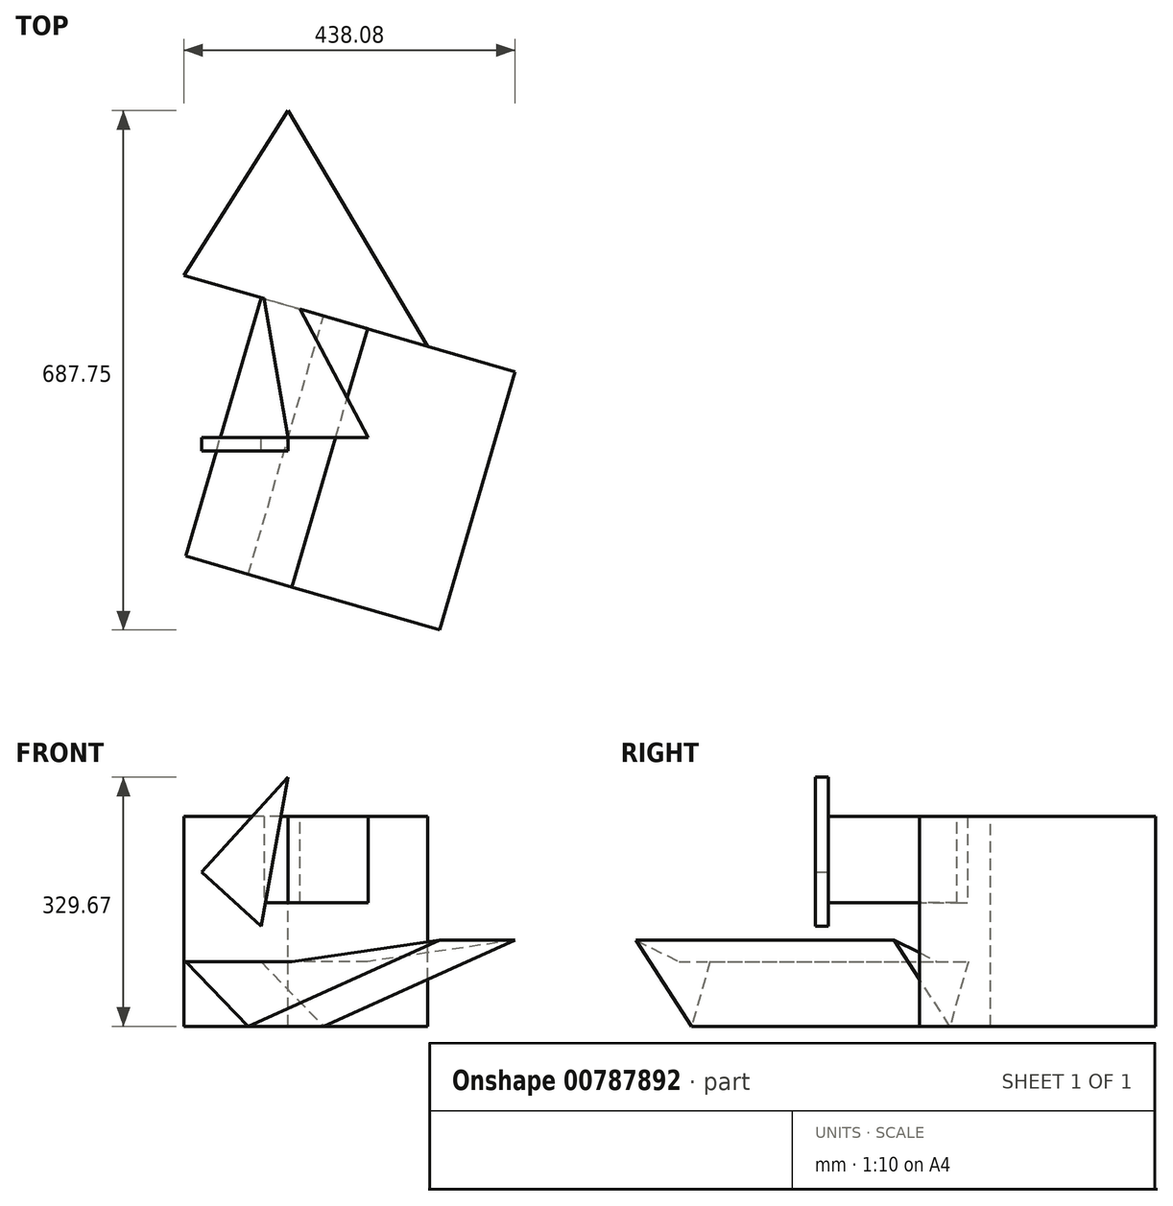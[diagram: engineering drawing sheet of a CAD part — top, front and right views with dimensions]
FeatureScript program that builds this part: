
annotation { "Feature Type Name" : "Feature", "Feature Type Description" : "" }
export const myFeature = defineFeature(function(context is Context, id is Id, definition is map)
    precondition{}
    {
        {
            var Q0;
            Q0=qCreatedBy(makeId("Front.planeOp"),FACE);
            var sketch = newSketch(context, id + "F0", { "sketchPlane" : qUnion([Q0])});
            skLineSegment(sketch, "E0", {"start": v(0, 166.37) * mm, "end": v(-114.51, 40.95) * mm});
            skLineSegment(sketch, "E1", {"start": v(-114.51, 40.95) * mm, "end": v(-35.9, -30.84) * mm});
            skLineSegment(sketch, "E2", {"start": v(-35.9, -30.84) * mm, "end": v(0, 166.37) * mm});
            skSolve(sketch);
        }
        {
            var Q0;
            Q0 = qSketchRegion(id + "F0", true);
            extrude(context, id + "F1", {"entities" : qUnion([Q0]), "depth" : 17.63 * mm, "offsetDistance" : 25.4 * mm});
        }
        {
            var Q0;
            Q0=qCreatedBy(makeId("Top.planeOp"),FACE);
            var sketch = newSketch(context, id + "F2", { "sketchPlane" : qUnion([Q0])});
            skLineSegment(sketch, "E3", {"start": v(0, 0) * mm, "end": v(-51.73, 296.94) * mm});
            skLineSegment(sketch, "E4", {"start": v(-51.73, 296.94) * mm, "end": v(105.96, 0) * mm});
            skLineSegment(sketch, "E5", {"start": v(105.96, 0) * mm, "end": v(0, 0) * mm});
            skSolve(sketch);
        }
        {
            var Q0;
            Q0 = qSketchRegion(id + "F2", true);
            extrude(context, id + "F3", {"entities" : qUnion([Q0]), "depth" : 114.27 * mm, "offsetDistance" : 25.4 * mm});
        }
        {
            var Q0;
            Q0=makeQuery(id+"F3.opExtrude","CAP_FACE",FACE,{"disambiguationData":[OSD([sQuery(id+"F2.wireOp",EDGE,"E3"),sQuery(id+"F2.wireOp",EDGE,"E4"),sQuery(id+"F2.wireOp",EDGE,"E5")])],"isStart":false});
            var sketch = newSketch(context, id + "F4", { "sketchPlane" : qUnion([Q0])});
            skLineSegment(sketch, "E6", {"start": v(0, 432.82) * mm, "end": v(184.6, 120.56) * mm});
            skLineSegment(sketch, "E7", {"start": v(184.6, 120.56) * mm, "end": v(-137.93, 214.74) * mm});
            skLineSegment(sketch, "E8", {"start": v(-137.93, 214.74) * mm, "end": v(0, 432.82) * mm});
            skSolve(sketch);
        }
        {
            var Q0;
            Q0 = qSketchRegion(id + "F4", true);
            extrude(context, id + "F5", {"entities" : qUnion([Q0]), "operationType" : NewBodyOperationType.ADD, "oppositeDirection" : true, "depth" : 277.57 * mm, "offsetDistance" : 25.4 * mm});
        }
        {
            var Q0;
            Q0=makeQuery(id+"F5.opExtrude","SWEPT_FACE",FACE,{"disambiguationData":[OSD([sQuery(id+"F4.wireOp",EDGE,"E7")])]});
            var sketch = newSketch(context, id + "F6", { "sketchPlane" : qUnion([Q0])});
            skLineSegment(sketch, "E9", {"start": v(207.2, -77.56) * mm, "end": v(-86.2, -77.56) * mm});
            skLineSegment(sketch, "E10", {"start": v(-86.2, -77.56) * mm, "end": v(0, -163.3) * mm});
            skLineSegment(sketch, "E11", {"start": v(0, -163.3) * mm, "end": v(263.78, -49.33) * mm});
            skLineSegment(sketch, "E12", {"start": v(263.78, -49.33) * mm, "end": v(60.5, -77.56) * mm});
            skSolve(sketch);
        }
        {
            var Q0;
            Q0 = qSketchRegion(id + "F6", true);
            var Q1;
            {var subQ1=sQuery(id+"F6.wireOp",EDGE,"E10");Q1=makeQuery(id+"F6.imprint","IMPRINT",FACE,{"disambiguationData":[TD([[makeQuery(id+"F6.imprint","IMPRINT",EDGE,{"derivedFrom":subQ1}),1.0]])]});}
            extrude(context, id + "F7", {"entities" : qUnion([Q0, Q1]), "operationType" : NewBodyOperationType.ADD, "depth" : 356.02 * mm, "offsetDistance" : 25.4 * mm});
        }
    });
